# Revit family: Burns_&_Ferrall_-_Sink_-_Aquis_Integrato_Double
name_source: partatom
category: Plumbing Fixtures
revit_build: Autodesk Revit 2014 (Build: 20140709_2115(x64)
units: mm (PartAtom-declared; Revit-internal decimal feet)

## types (3) — shared parameters
Depth = 410 mm  [stored 1.34514 ft]
Description = Bowl 350x300x150, 40 waste
Drain Diamter = 80 mm  [stored 0.262467 ft]
Drain Position = 100 mm  [stored 0.328084 ft]
Flange = 25 mm  [stored 0.082021 ft]
Height = 215 mm
Manufacturer = Burns Ferrall
Material = Stainless Steel
Material Thickness = 2 mm  [stored 0.00656168 ft]
Model = Integrato Double
Overall Depth = 460 mm  [stored 1.50919 ft]
Radius = 10 mm  [stored 0.0328084 ft]
URL = https://productspec.net

## per-type parameters (varying)
| type | Overall Width | Width 1 | Width 2 |
| INB400D | 853 mm  [stored 2.79856 ft] | 400 mm  [stored 1.31234 ft] | 400 mm  [stored 1.31234 ft] |
| INB450DLH | 750 mm  [stored 2.46063 ft] | 247 mm | 450 mm  [stored 1.47638 ft] |
| INB450DRH | 750 mm  [stored 2.46063 ft] | 450 mm  [stored 1.47638 ft] | 247 mm |

note: [stored X ft] marks values corroborated as IEEE doubles in the binary element streams (Revit-internal decimal feet)

## geometry (parser evidence)
native form markers: Blend x4, Sweep x4
no freeform markers — native parametric forms only
